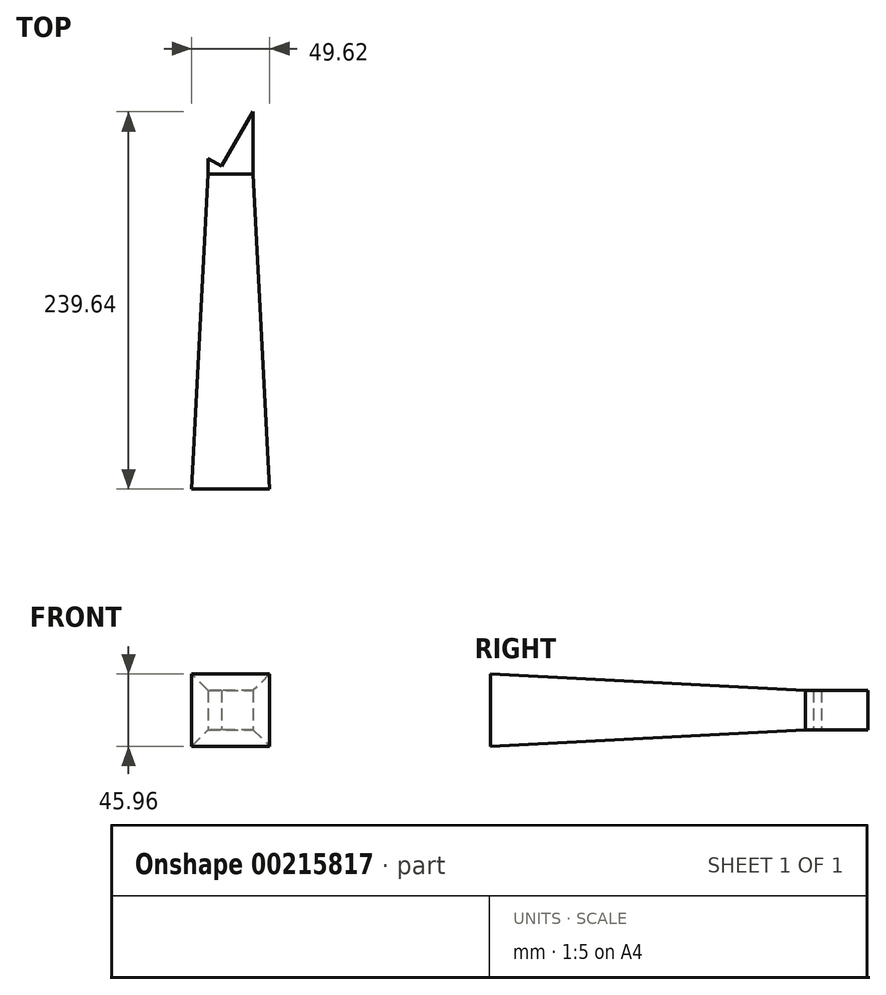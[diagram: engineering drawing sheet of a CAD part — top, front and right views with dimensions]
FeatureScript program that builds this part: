
annotation { "Feature Type Name" : "Feature", "Feature Type Description" : "" }
export const myFeature = defineFeature(function(context is Context, id is Id, definition is map)
    precondition{}
    {
        {
            var Q0;
            Q0=qCreatedBy(makeId("Top.planeOp"),FACE);
            var sketch = newSketch(context, id + "F0", { "sketchPlane" : qUnion([Q0])});
            skLineSegment(sketch, "E0", {"start": v(0, 0) * mm, "end": v(28.66, 0) * mm});
            skLineSegment(sketch, "E1", {"start": v(28.66, 0) * mm, "end": v(28.66, 39.64) * mm});
            skLineSegment(sketch, "E2", {"start": v(28.66, 39.64) * mm, "end": v(8.66, 5) * mm});
            skLineSegment(sketch, "E3", {"start": v(8.66, 5) * mm, "end": v(0, 10) * mm});
            skLineSegment(sketch, "E4", {"start": v(0, 10) * mm, "end": v(0, 0) * mm});
            skSolve(sketch);
        }
        {
            var Q0;
            Q0 = qSketchRegion(id + "F0", true);
            extrude(context, id + "F1", {"entities" : qUnion([Q0]), "depth" : 25 * mm});
        }
        {
            var Q0;
            Q0=makeQuery(id+"F1.opExtrude","SWEPT_FACE",FACE,{"disambiguationData":[OSD([sQuery(id+"F0.wireOp",EDGE,"E0")])]});
            var sketch = newSketch(context, id + "F2", { "sketchPlane" : qUnion([Q0])});
            skSolve(sketch);
        }
        {
            var Q0;
            Q0 = qSketchRegion(id + "F2", true);
            var Q1;
            {var subQ0=sQuery(id+"F0.wireOp",EDGE,"E0");Q1=makeQuery(id+"F2.imprint","IMPRINT",FACE,{"disambiguationData":[TD([[makeQuery(id+"F2.imprint","IMPRINT",EDGE,{"derivedFrom":makeQuery(id+"F1.opExtrude","CAP_EDGE",EDGE,{"disambiguationData":[OSD([subQ0])],"isStart":true})}),1.0]])]});}
            extrude(context, id + "F3", {"entities" : qUnion([Q0, Q1]), "operationType" : NewBodyOperationType.ADD, "depth" : 200 * mm, "hasDraft" : true, "draftAngle" : 3 * degree});
        }
    });
